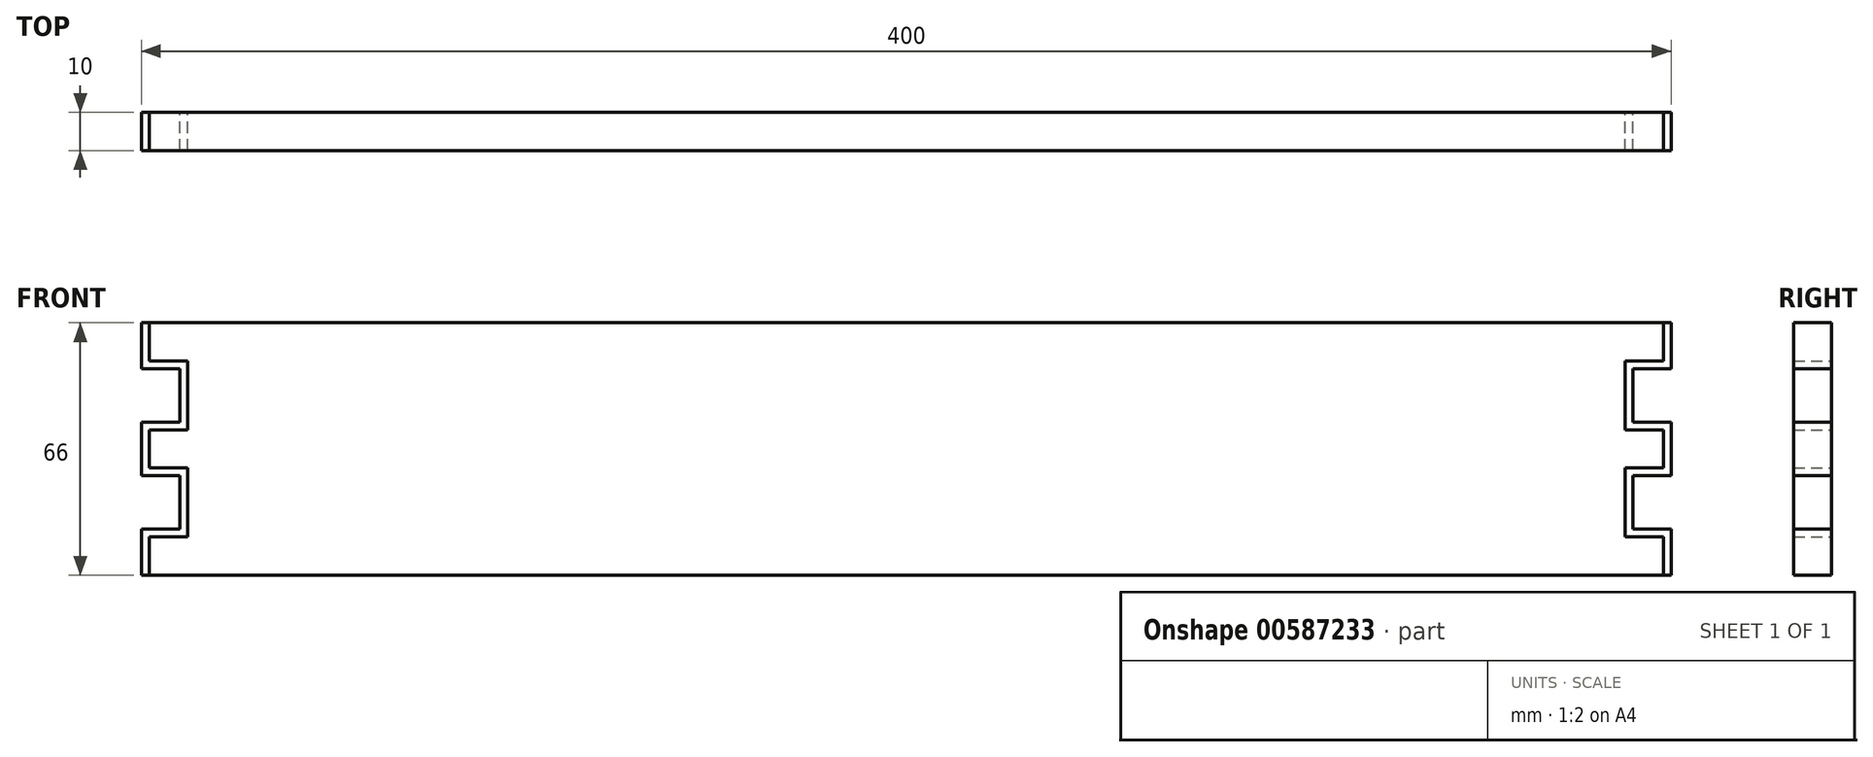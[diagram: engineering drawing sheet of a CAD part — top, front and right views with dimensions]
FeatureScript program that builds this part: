
annotation { "Feature Type Name" : "Feature", "Feature Type Description" : "" }
export const myFeature = defineFeature(function(context is Context, id is Id, definition is map)
    precondition{}
    {
        {
            assignVariable(context, id + "F0", {"name" : "BitSz", "anyValue" : 10});
        }
        {
            var Q0;
            Q0=qCreatedBy(makeId("Front.planeOp"),FACE);
            var sketch = newSketch(context, id + "F1", { "sketchPlane" : qUnion([Q0])});
            skLineSegment(sketch, "E0", {"start": v(0, 0) * mm, "end": v(0, 10) * mm});
            skLineSegment(sketch, "E1", {"start": v(0, 10) * mm, "end": v(10, 10) * mm});
            skLineSegment(sketch, "E2", {"start": v(10, 10) * mm, "end": v(10, 28) * mm});
            skLineSegment(sketch, "E3", {"start": v(10, 28) * mm, "end": v(0, 28) * mm});
            skLineSegment(sketch, "E4", {"start": v(0, 28) * mm, "end": v(0, 38) * mm});
            skLineSegment(sketch, "E5", {"start": v(0, 38) * mm, "end": v(10, 38) * mm});
            skLineSegment(sketch, "E6", {"start": v(10, 38) * mm, "end": v(10, 56) * mm});
            skLineSegment(sketch, "E7", {"start": v(10, 56) * mm, "end": v(0, 56) * mm});
            skLineSegment(sketch, "E8", {"start": v(0, 56) * mm, "end": v(0, 66) * mm});
            skLineSegment(sketch, "E9", {"start": v(0, 66) * mm, "end": v(198, 66) * mm});
            skLineSegment(sketch, "E10", {"start": v(198, 0) * mm, "end": v(0, 0) * mm});
            skLineSegment(sketch, "E11", {"start": v(198, 0) * mm, "end": v(198, 66) * mm, "construction": true});
            skLineSegment(sketch, "E12.0", {"start": v(-2, 54) * mm, "end": v(-2, 66) * mm});
            skLineSegment(sketch, "E12.1", {"start": v(8, 54) * mm, "end": v(-2, 54) * mm});
            skLineSegment(sketch, "E12.2", {"start": v(8, 40) * mm, "end": v(8, 54) * mm});
            skLineSegment(sketch, "E12.3", {"start": v(-2, 40) * mm, "end": v(8, 40) * mm});
            skLineSegment(sketch, "E12.4", {"start": v(-2, 26) * mm, "end": v(-2, 40) * mm});
            skLineSegment(sketch, "E12.5", {"start": v(-2, 0) * mm, "end": v(-2, 12) * mm});
            skLineSegment(sketch, "E12.6", {"start": v(-2, 12) * mm, "end": v(8, 12) * mm});
            skLineSegment(sketch, "E12.7", {"start": v(8, 12) * mm, "end": v(8, 26) * mm});
            skLineSegment(sketch, "E12.8", {"start": v(8, 26) * mm, "end": v(-2, 26) * mm});
            skLineSegment(sketch, "E13", {"start": v(-2, 66) * mm, "end": v(0, 66) * mm});
            skLineSegment(sketch, "E14", {"start": v(-2, 0) * mm, "end": v(0, 0) * mm});
            skLineSegment(sketch, "E15.MirrorCS", {"start": v(398, 66) * mm, "end": v(396, 66) * mm});
            skLineSegment(sketch, "E16.MirrorCS", {"start": v(398, 0) * mm, "end": v(396, 0) * mm});
            skLineSegment(sketch, "E17.MirrorCS", {"start": v(396, 56) * mm, "end": v(396, 66) * mm});
            skLineSegment(sketch, "E18.MirrorCS", {"start": v(386, 56) * mm, "end": v(396, 56) * mm});
            skLineSegment(sketch, "E19.MirrorCS", {"start": v(386, 10) * mm, "end": v(386, 28) * mm});
            skLineSegment(sketch, "E20.MirrorCS", {"start": v(396, 66) * mm, "end": v(198, 66) * mm});
            skLineSegment(sketch, "E21.MirrorCS", {"start": v(386, 28) * mm, "end": v(396, 28) * mm});
            skLineSegment(sketch, "E22.MirrorCS", {"start": v(398, 0) * mm, "end": v(398, 12) * mm});
            skLineSegment(sketch, "E23.MirrorCS", {"start": v(396, 28) * mm, "end": v(396, 38) * mm});
            skLineSegment(sketch, "E24.MirrorCS", {"start": v(398, 12) * mm, "end": v(388, 12) * mm});
            skLineSegment(sketch, "E25.MirrorCS", {"start": v(198, 0) * mm, "end": v(396, 0) * mm});
            skLineSegment(sketch, "E26.MirrorCS", {"start": v(388, 12) * mm, "end": v(388, 26) * mm});
            skLineSegment(sketch, "E27.MirrorCS", {"start": v(386, 38) * mm, "end": v(386, 56) * mm});
            skLineSegment(sketch, "E28.MirrorCS", {"start": v(398, 54) * mm, "end": v(398, 66) * mm});
            skLineSegment(sketch, "E29.MirrorCS", {"start": v(388, 26) * mm, "end": v(398, 26) * mm});
            skLineSegment(sketch, "E30.MirrorCS", {"start": v(398, 40) * mm, "end": v(388, 40) * mm});
            skLineSegment(sketch, "E31.MirrorCS", {"start": v(388, 40) * mm, "end": v(388, 54) * mm});
            skLineSegment(sketch, "E32.MirrorCS", {"start": v(398, 26) * mm, "end": v(398, 40) * mm});
            skLineSegment(sketch, "E33.MirrorCS", {"start": v(396, 0) * mm, "end": v(396, 10) * mm});
            skLineSegment(sketch, "E34.MirrorCS", {"start": v(388, 54) * mm, "end": v(398, 54) * mm});
            skLineSegment(sketch, "E35.MirrorCS", {"start": v(396, 10) * mm, "end": v(386, 10) * mm});
            skLineSegment(sketch, "E36.MirrorCS", {"start": v(396, 38) * mm, "end": v(386, 38) * mm});
            skSolve(sketch);
        }
        {
            var Q0;
            Q0=makeQuery(id+"F1.imprint","IMPRINT",FACE,{"disambiguationData":[TD([[makeQuery(id+"F1.imprint","IMPRINT",EDGE,{"derivedFrom":sQuery(id+"F1.wireOp",EDGE,"E0")}),-1.0]])]});
            extrude(context, id + "F2", {"entities" : qUnion([Q0]), "endBound" : BoundingType.SYMMETRIC, "depth" : (getVariable(context, 'BitSz')) * mm, "offsetDistance" : 25 * mm});
        }
        {
            var Q0;
            Q0=makeQuery(id+"F1.imprint","IMPRINT",FACE,{"disambiguationData":[TD([[makeQuery(id+"F1.imprint","IMPRINT",EDGE,{"derivedFrom":sQuery(id+"F1.wireOp",EDGE,"E0")}),1.0]])]});
            var Q1;
            Q1=makeQuery(id+"F1.imprint","IMPRINT",FACE,{"disambiguationData":[TD([[makeQuery(id+"F1.imprint","IMPRINT",EDGE,{"derivedFrom":sQuery(id+"F1.wireOp",EDGE,"E15.MirrorCS")}),1.0]])]});
            extrude(context, id + "F3", {"entities" : qUnion([Q0, Q1]), "endBound" : BoundingType.SYMMETRIC, "depth" : (getVariable(context, 'BitSz')) * mm, "offsetDistance" : 25 * mm});
        }
    });
